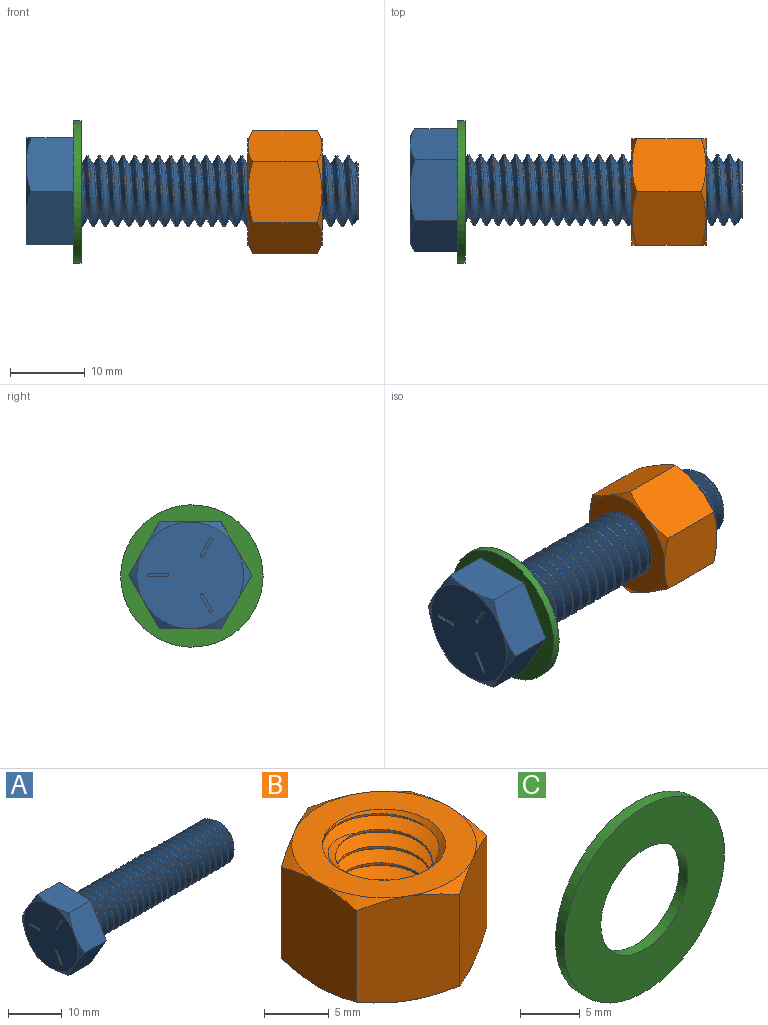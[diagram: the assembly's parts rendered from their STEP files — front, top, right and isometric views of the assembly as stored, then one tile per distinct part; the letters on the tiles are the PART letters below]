
ASSEMBLY  parts=3 mates=2
PART A: 35 faces, bbox 45.9x17.2x17.2 mm
  f0: plane 8.94x7.03mm, normal (0,0,1), area 50.6mm2, adj f1,f5,f12,f13,f18
  f1: plane 7.82x7.03mm, normal (0,0.87,0.5), area 50.6mm2, adj f0,f2,f12,f17,f18
  f2: plane 7.82x7.03mm, normal (0,0.87,-0.5), area 50.6mm2, adj f1,f3,f12,f16,f17
  f3: plane 8.94x7.03mm, normal (0,0,-1), area 50.6mm2, adj f2,f4,f12,f15,f16
  f4: plane 7.82x7.03mm, normal (0,-0.87,-0.5), area 50.6mm2, adj f3,f5,f12,f14,f15
  f5: plane 7.82x7.03mm, normal (0,-0.87,0.5), area 50.6mm2, adj f0,f4,f12,f13,f14
  f6: cylinder r=4.76mm len=37.13mm, axis (1,0,0), area 138.9mm2, adj f8,f10,f11,f12
  f7: plane 7.6x7.57mm, normal (1,0,0), area 44.9mm2, adj f8,f9,f10,f11
  f8: cone r=3.79mm half-angle=45deg, axis (-1,0,0), area 17.1mm2, adj f6,f7,f10,f11
  f9: bspline ~38.7x7.46mm, area 111.5mm2, adj f7,f10,f11,f12
  f10: bspline ~38.89x9.53mm, area 752.7mm2, adj f6,f7,f8,f9,f12
  f11: bspline ~39.49x9.53mm, area 754mm2, adj f6,f7,f8,f9,f12
  f12: plane 16.52x14.31mm, normal (1,0,0), area 119.7mm2, adj f0,f1,f2,f3,f4,f5,f6,f9
  f13: cone r=7.14mm half-angle=60deg, axis (1,0,0), area 5mm2, adj f0,f5,f19
  f14: cone r=7.14mm half-angle=60deg, axis (1,0,0), area 5mm2, adj f4,f5,f19
  f15: cone r=7.14mm half-angle=60deg, axis (1,0,0), area 5mm2, adj f3,f4,f19
  f16: cone r=7.14mm half-angle=60deg, axis (1,0,0), area 5mm2, adj f2,f3,f19
  f17: cone r=7.14mm half-angle=60deg, axis (1,0,0), area 5mm2, adj f1,f2,f19
  f18: cone r=7.14mm half-angle=60deg, axis (1,0,0), area 5mm2, adj f0,f1,f19
  f19: plane 14.29x14.29mm, normal (-1,0,0), area 156.8mm2, adj f13,f14,f15,f16,f17,f18,f20,f21
  f20: cylinder r=0.21mm len=0.43mm, axis (-1,0,0), area 0.2mm2, adj f19,f21,f23,f24
  f21: plane 2.43x0.25mm, normal (0,0,-1), area 0.6mm2, adj f19,f20,f22,f24
  f22: cylinder r=0.21mm len=0.43mm, axis (-1,0,0), area 0.2mm2, adj f19,f21,f23,f24
  f23: plane 2.43x0.25mm, normal (0,0,1), area 0.6mm2, adj f19,f20,f22,f24
  f24: plane 2.86x0.43mm, normal (-1,0,0), area 1.2mm2, adj f20,f21,f22,f23
  f25: cylinder r=0.21mm len=0.4mm, axis (-1,0,0), area 0.2mm2, adj f19,f26,f28,f29
  f26: plane 2.1x1.21mm, normal (0,0.87,0.5), area 0.6mm2, adj f19,f25,f27,f29
  f27: cylinder r=0.21mm len=0.4mm, axis (-1,0,0), area 0.2mm2, adj f19,f26,f28,f29
  f28: plane 2.1x1.21mm, normal (0,-0.87,-0.5), area 0.6mm2, adj f19,f25,f27,f29
  f29: plane 2.53x1.64mm, normal (-1,0,0), area 1.2mm2, adj f25,f26,f27,f28
  f30: cylinder r=0.21mm len=0.4mm, axis (-1,0,0), area 0.2mm2, adj f19,f31,f33,f34
  f31: plane 2.1x1.21mm, normal (0,-0.87,0.5), area 0.6mm2, adj f19,f30,f32,f34
  f32: cylinder r=0.21mm len=0.4mm, axis (-1,0,0), area 0.2mm2, adj f19,f31,f33,f34
  f33: plane 2.1x1.21mm, normal (0,0.87,-0.5), area 0.6mm2, adj f19,f30,f32,f34
  f34: plane 2.53x1.64mm, normal (-1,0,0), area 1.2mm2, adj f30,f31,f32,f33
PART B: 26 faces, bbox 17.2x17.2x11.8 mm
  f0: plane 14.29x14.29mm, normal (0,0,1), area 89.1mm2, adj f7,f12,f13,f14,f15,f16,f17,f18
  f1: plane 10.61x7.82mm, normal (-0.5,0.87,0), area 78.2mm2, adj f2,f6,f13,f18,f21,f22
  f2: plane 10.61x8.94mm, normal (-1,0,0), area 78.2mm2, adj f1,f3,f17,f18,f22,f23
  f3: plane 10.61x7.82mm, normal (-0.5,-0.87,0), area 78.2mm2, adj f2,f4,f16,f17,f23,f24
  f4: plane 10.61x7.82mm, normal (0.5,-0.87,0), area 78.2mm2, adj f3,f5,f15,f16,f24,f25
  f5: plane 10.61x8.94mm, normal (1,0,0), area 78.2mm2, adj f4,f6,f14,f15,f20,f25
  f6: plane 10.61x7.82mm, normal (0.5,0.87,0), area 78.2mm2, adj f1,f5,f13,f14,f20,f21
  f7: cylinder r=4.76mm len=9.92mm, axis (0,0,-1), area 37.2mm2, adj f0,f8,f9,f11
  f8: plane 14.29x14.29mm, normal (0,0,-1), area 89.1mm2, adj f7,f19,f20,f21,f22,f23,f24,f25
  f9: bspline ~10.72x9.53mm, area 179.1mm2, adj f7,f10,f12,f19
  f10: bspline ~8.33x7.46mm, area 22.8mm2, adj f9,f11,f12,f19
  f11: bspline ~10.52x9.53mm, area 177.8mm2, adj f7,f10,f12,f19
  f12: cone r=4.37mm half-angle=45deg, axis (0,0,1), area 20mm2, adj f0,f9,f10,f11
  f13: cone r=7.14mm half-angle=60deg, axis (0,0,-1), area 5mm2, adj f0,f1,f6
  f14: cone r=7.14mm half-angle=60deg, axis (0,0,-1), area 5mm2, adj f0,f5,f6
  f15: cone r=7.14mm half-angle=60deg, axis (0,0,-1), area 5mm2, adj f0,f4,f5
  f16: cone r=7.14mm half-angle=60deg, axis (0,0,-1), area 5mm2, adj f0,f3,f4
  f17: cone r=7.14mm half-angle=60deg, axis (0,0,-1), area 5mm2, adj f0,f2,f3
  f18: cone r=7.14mm half-angle=60deg, axis (0,0,-1), area 5mm2, adj f0,f1,f2
  f19: cone r=4.37mm half-angle=45deg, axis (0,0,-1), area 20mm2, adj f8,f9,f10,f11
  f20: cone r=7.14mm half-angle=60deg, axis (0,0,1), area 5mm2, adj f5,f6,f8
  f21: cone r=7.14mm half-angle=60deg, axis (0,0,1), area 5mm2, adj f1,f6,f8
  f22: cone r=7.14mm half-angle=60deg, axis (0,0,1), area 5mm2, adj f1,f2,f8
  f23: cone r=7.14mm half-angle=60deg, axis (0,0,1), area 5mm2, adj f2,f3,f8
  f24: cone r=7.14mm half-angle=60deg, axis (0,0,1), area 5mm2, adj f3,f4,f8
  f25: cone r=7.14mm half-angle=60deg, axis (0,0,1), area 5mm2, adj f4,f5,f8
PART C: 4 faces, bbox 19.1x1x19.1 mm
  f0: cylinder r=9.53mm len=19.05mm, axis (0,-1,0), area 60.8mm2, adj f1,f2
  f1: plane 19.05x19.05mm, normal (0,1,0), area 201.5mm2, adj f0,f3
  f2: plane 19.05x19.05mm, normal (0,-1,0), area 201.5mm2, adj f0,f3
  f3: cylinder r=5.16mm len=10.31mm, axis (0,1,0), area 32.9mm2, adj f1,f2
PLACE A at identity fixed
PLACE B rot(axis=(0.58,-0.58,-0.58),120deg) t=(12.45,-0.23,-0.09)mm
PLACE C rot(axis=(0.58,0.58,-0.58),120deg) t=(-15.88,-0.23,-0.09)mm
MATE fastened B.f12 <-> C.f0  axis (-1,0,0) through (7.49,-0.23,-0.09)mm
MATE fastened C.f0 <-> A.f12  axis (-1,0,0) through (-15.88,-0.23,-0.09)mm
